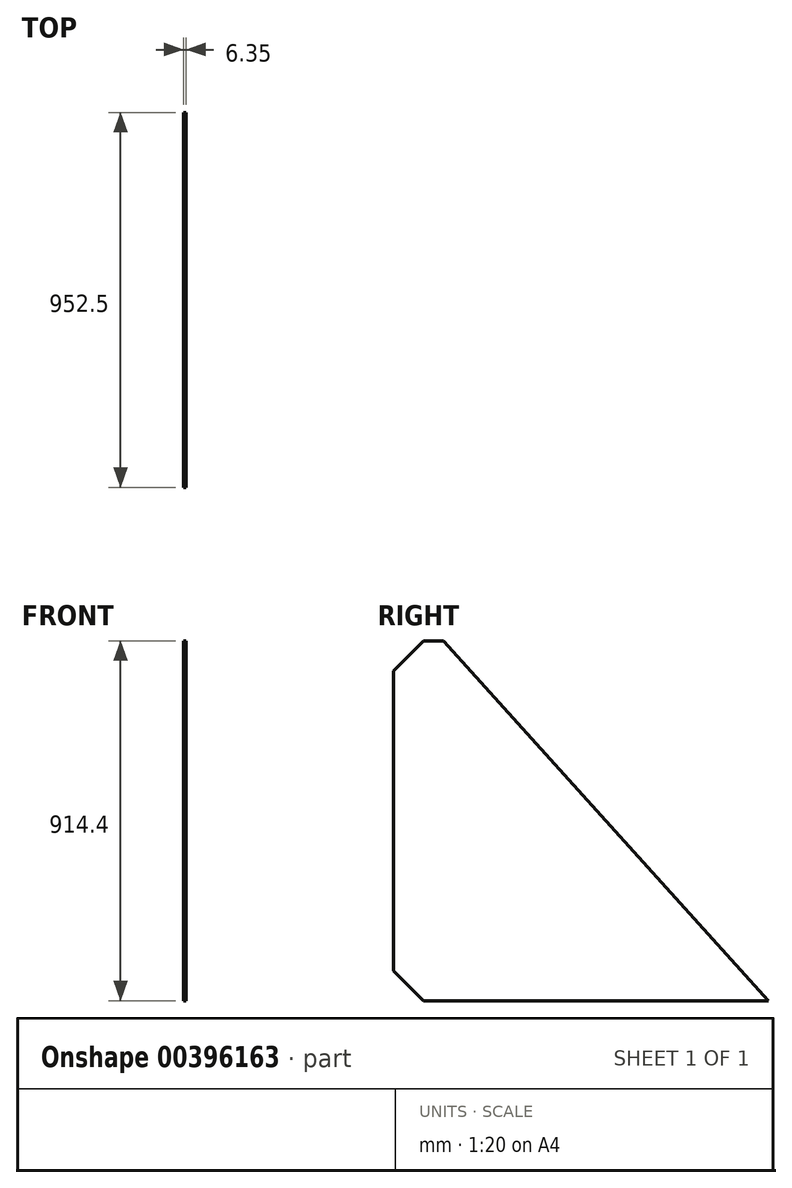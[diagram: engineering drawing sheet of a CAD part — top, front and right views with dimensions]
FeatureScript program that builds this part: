
annotation { "Feature Type Name" : "Feature", "Feature Type Description" : "" }
export const myFeature = defineFeature(function(context is Context, id is Id, definition is map)
    precondition{}
    {
        {
            var Q0;
            Q0=qCreatedBy(makeId("Right.planeOp"),FACE);
            var sketch = newSketch(context, id + "F0", { "sketchPlane" : qUnion([Q0])});
            skLineSegment(sketch, "E0", {"start": v(-432.47, 363.98) * mm, "end": v(-432.47, -398.02) * mm});
            skLineSegment(sketch, "E1", {"start": v(-432.47, -398.02) * mm, "end": v(-356.27, -474.22) * mm});
            skLineSegment(sketch, "E2", {"start": v(-356.27, -474.22) * mm, "end": v(520.03, -474.22) * mm});
            skLineSegment(sketch, "E3", {"start": v(520.03, -474.22) * mm, "end": v(-305.47, 440.18) * mm});
            skLineSegment(sketch, "E4", {"start": v(-305.47, 440.18) * mm, "end": v(-356.27, 440.18) * mm});
            skLineSegment(sketch, "E5", {"start": v(-356.27, 440.18) * mm, "end": v(-432.47, 363.98) * mm});
            skSolve(sketch);
        }
        {
            var Q0;
            Q0=makeQuery(id+"F0.imprint","IMPRINT",FACE,{"disambiguationData":[TD([[makeQuery(id+"F0.imprint","IMPRINT",EDGE,{"derivedFrom":sQuery(id+"F0.wireOp",EDGE,"E0")}),1.0]])]});
            extrude(context, id + "F1", {"entities" : qUnion([Q0]), "depth" : 6.35 * mm});
        }
    });
